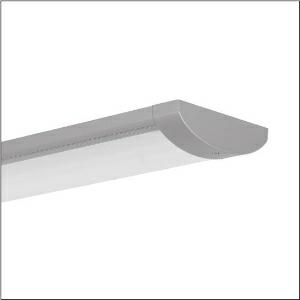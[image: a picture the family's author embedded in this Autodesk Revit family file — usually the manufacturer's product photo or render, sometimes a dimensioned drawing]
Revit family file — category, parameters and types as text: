
# Revit family: tv_20_5xa861d2n0a
name_source: partatom
category: Lighting Fixtures
units: mm (PartAtom-declared; Revit-internal decimal feet)

## family parameters
Cut with Voids When Loaded = No
Host = Face
Light Source = No
Part Type = Normal
Room Calculation Point = No
Round Connector Dimension = Use Diameter
Shared = No

## types (1)
- TV 20 (1 x LED 4000K / CRI = 80 (unbekannt), 2130 lm, 4000K)
    Apparent Load = 21 VA
    CIE Flux Codes = 48 78 95 99 100
    Color Rendering = 80
    Color Temperature = 4000K
    Default Elevation = 1800 mm
    Description = TV 20, vandal-proof luminaire, primary light control with specular reflector, of aluminium, matt, primary optical cover: enclosure, of PC, frosted, light emission: direct distribution, primary light characteristic: symmetric, installation type: surface-mounted, LED, rated luminous flux: 2.130lm, luminous efficacy: 101lm/W, light colour: 840, colour temperature: 4000K, control gear: DALI, mains connection: 230V, AC, 50Hz, rated input power: 21W, luminaire housing, of aluminium, coated, SITECO metallic grey (DB 702S), with wall and ceiling fixing element, length: 705mm, width: 260mm, height: 70mm, mounting height: 2.5..4.0m, protection rating (complete): IP65, insulation class (complete): insulation class I (protective earthing), certification: CE, protection symbol: F, impact resistance: 2x IK10, standard: EN 60598, packaging unit: 1 piece
    Height = 70 mm
    Lamp = 1 x LED 4000K / CRI >= 80 (unbekannt)
    Lamp Light Flux = 2130 lm
    Lamp count = 1
    Length = 705 mm
    Luminous efficacy = 101 lm/W
    Manufacturer = Siteco
    ModVariant = No
    Model = 5XA861D2N0A
    Mounting Place = Ceiling
    Mounting Type = Surface mounted
    Number of Poles = 1
    OnlyDefault = Yes
    Power Factor = 1
    Product Name = TV 20
    Product group = vandal-proof luminaire
    ProductGroupID = 310
    Protection Class = Protection class I
    Protection Degree = IP 65
    RLX_Detail_Level = 1
    RLX_Emergency_Light_Flux = 0 lm
    RLX_Emergency_Type = 0
    RLX_Emergency_Type_DB = No
    RlxData = <blob elided: 34189 chars, md5=929dfd5a>
    Socket = socket
    Standby Power = 0 W
    System Light Flux = 2130 lm
    System Power = 21 W
    Type Comments = Product without accessories
    Type Image = l_1004809.jpg
    URL = http://relux.com
    VarID = ---
    Voltage = 0 V
    Weight = 0.00 kg
    Width = 260 mm

## geometry (parser evidence)
native form markers: Blend x4, Sweep x11
no freeform markers — native parametric forms only
